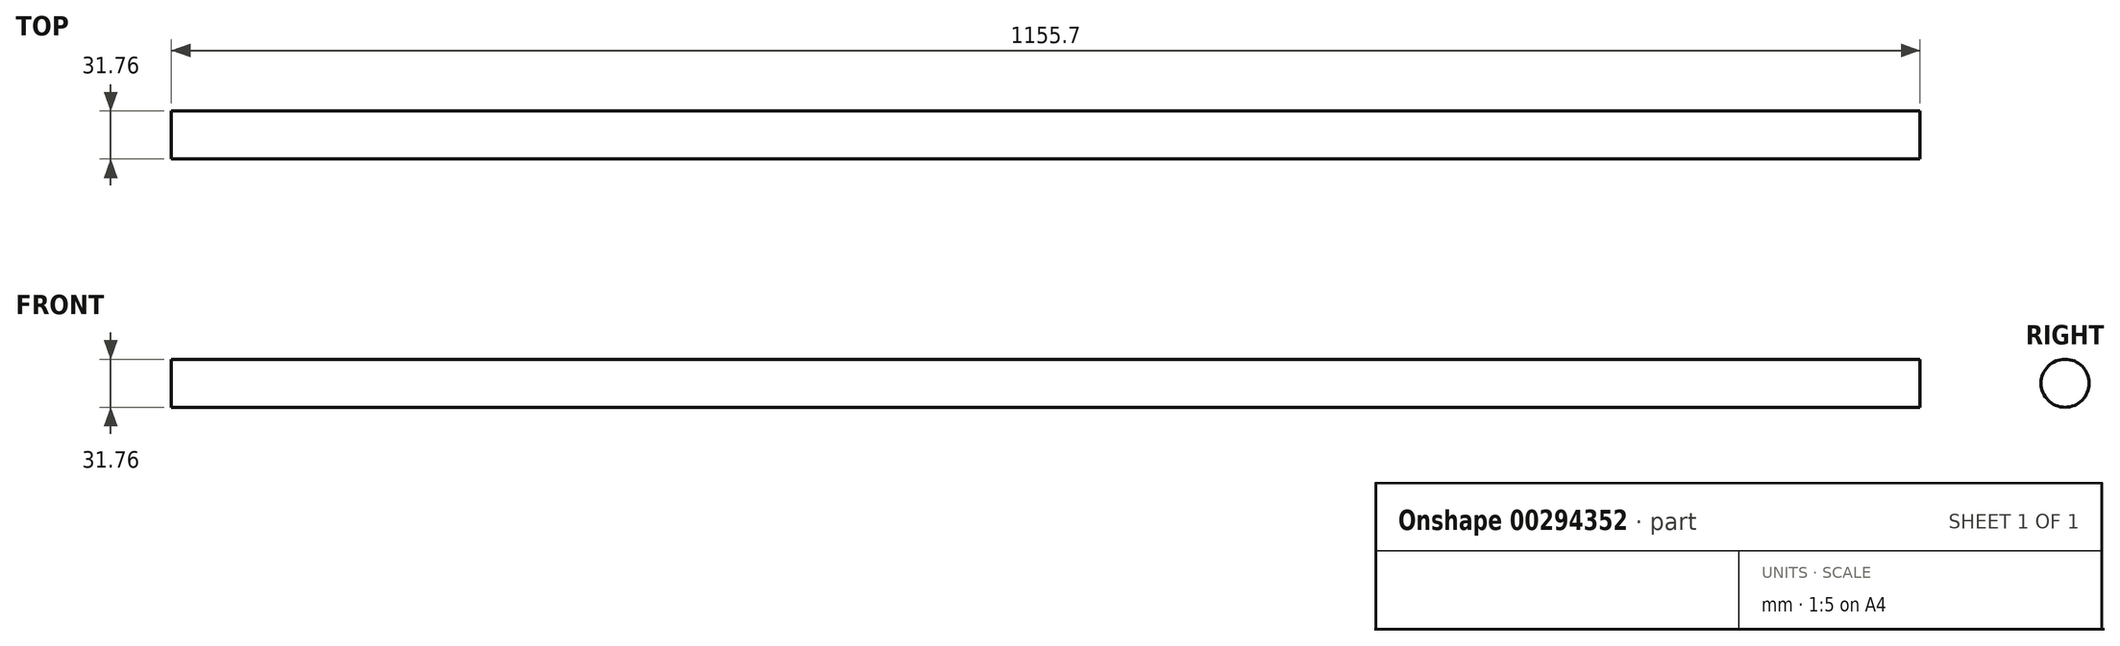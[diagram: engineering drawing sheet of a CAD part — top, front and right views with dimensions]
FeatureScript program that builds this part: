
annotation { "Feature Type Name" : "Feature", "Feature Type Description" : "" }
export const myFeature = defineFeature(function(context is Context, id is Id, definition is map)
    precondition{}
    {
        {
            var Q0;
            Q0=qCreatedBy(makeId("Right.planeOp"),FACE);
            var sketch = newSketch(context, id + "F0", { "sketchPlane" : qUnion([Q0])});
            skCircle(sketch, "E0", {"center": v(0, 0) * mm, "radius": 15.88 * mm});
            skSolve(sketch);
        }
        {
            var Q0;
            Q0 = qSketchRegion(id + "F0", true);
            extrude(context, id + "F1", {"entities" : qUnion([Q0]), "oppositeDirection" : true, "depth" : 1155.7 * mm});
        }
    });
